# Revit family: IFC_Каркас поддерживающий
name_source: partatom
category: Несущая арматура
units: mm (PartAtom-declared; Revit-internal decimal feet)

## family parameters
Всегда вертикально = Нет
На основе рабочей плоскости = Да
Общий = Да
При загрузке вырезать с полостями = Нет

## types (1)
- IFC_Каркас поддерживающий
    --- Наклонный стержень --- = --- Наклонный стержень ---
    --- Поперечный стержень --- = --- Поперечный стержень ---
    --- Продольный стержень --- = --- Продольный стержень ---
    ADSK_Арматура семейством = Да
    ADSK_Версия Revit = 2021
    ADSK_Версия семейства = 24.0221
    ADSK_Главная деталь изделия = Нет
    ADSK_Закладная деталь = Нет
    ADSK_Каркас = Да
    ADSK_Наименование_Текст1 = Каркас
    ADSK_Размер в погонных метрах = Нет
    Изображение типоразмера = <Нет>
    Каркас_Высота фиксации = 350 мм
    Каркас_Длина = 1500 мм
    Каркас_Шаг стержней = 500 мм
    Количество верхних стержней = 2
    Комментарии к типоразмеру = Каркас
    Массив_Количество = 4
    Наклонный стержень_Диаметр = 10 мм
    Наклонный стержень_Длина = 428 мм
    Наклонный стержень_Код металлопроката = 500
    Наклонный стержень_Материал = <По категории>
    Наклонный стержень_Пересечение = 345 мм
    Наклонный стержень_Смещение = 2 мм
    Наклонный стержень_Угол = 25.00°
    Наклонный стержень_Удлинение = 50 мм
    Отметка по умолчанию = 1219 мм
    Поперечный стержень_Диаметр = 10 мм
    Поперечный стержень_Длина = 322 мм
    Поперечный стержень_Код металлопроката = 500
    Поперечный стержень_Материал = <По категории>
    Поперечный стержень_Смещение = 10 мм
    Поперечный стержень_Удлинение = 0 мм
    Продолный стержень_Верх1 = Нет
    Продолный стержень_Верх2 = Да
    Продольный стержень_Верх1_Смещение = 19 мм
    Продольный стержень_Диаметр = 10 мм
    Продольный стержень_Код металлопроката = 500
    Продольный стержень_Материал = <По категории>
    Продольный стержень_Низ_Отступ = 50 мм
    Продольный стержень_Смещение = 10 мм
    Продольный стержень_Удлинение = 50 мм
    Срединный продольный стержень = Нет
